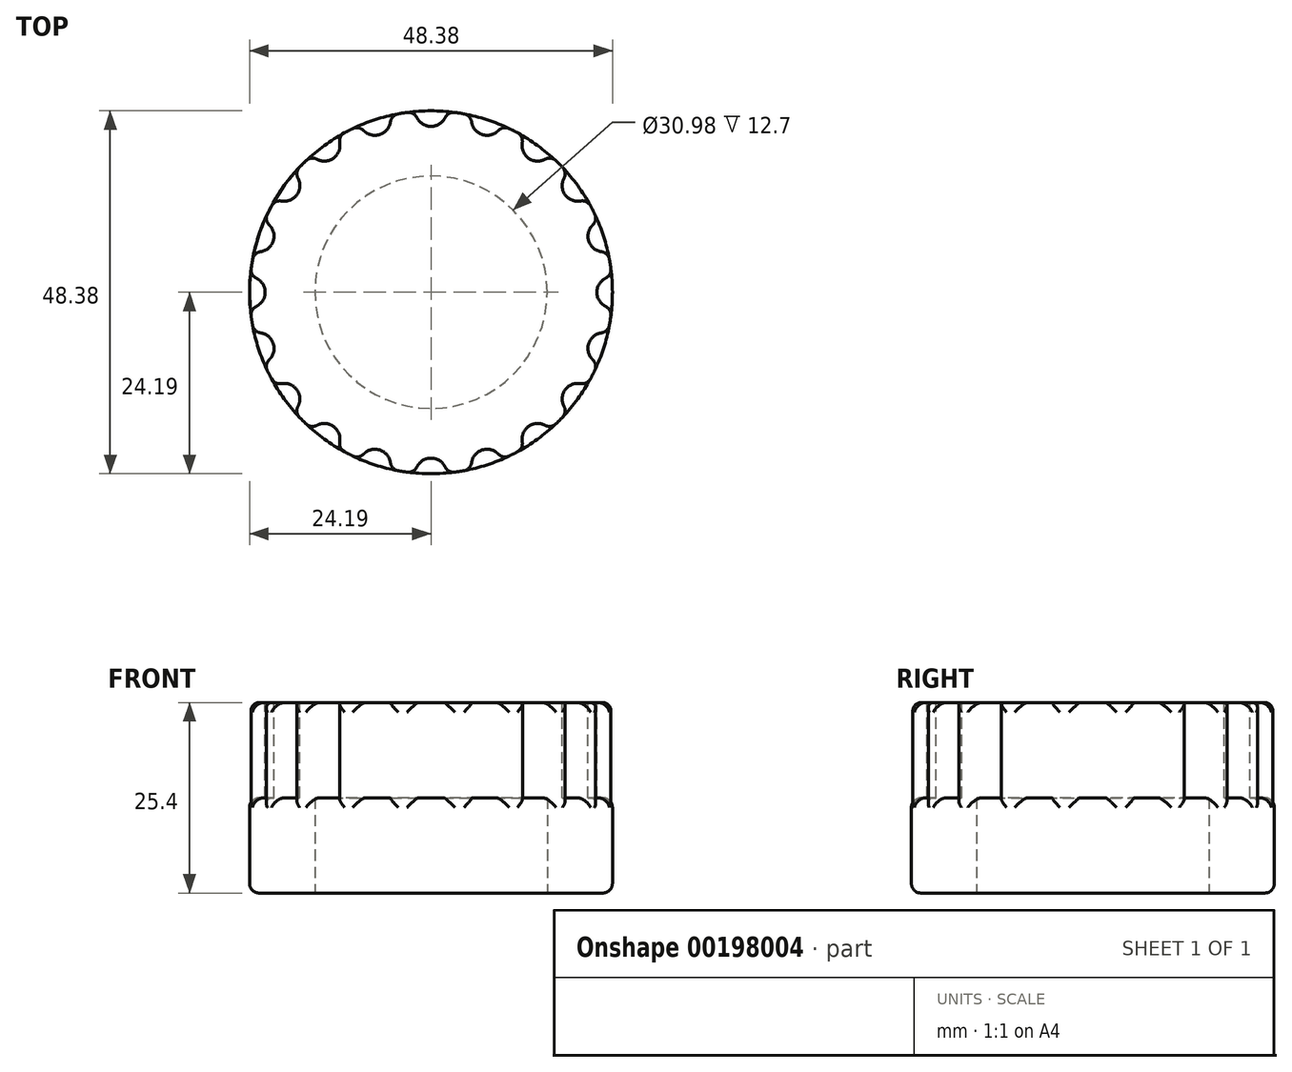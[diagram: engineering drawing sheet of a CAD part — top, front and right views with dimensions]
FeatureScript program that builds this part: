
annotation { "Feature Type Name" : "Feature", "Feature Type Description" : "" }
export const myFeature = defineFeature(function(context is Context, id is Id, definition is map)
    precondition{}
    {
        {
            var Q0;
            Q0=qCreatedBy(makeId("Top.planeOp"),FACE);
            var sketch = newSketch(context, id + "F0", { "sketchPlane" : qUnion([Q0])});
            skCircle(sketch, "E0", {"center": v(0, 0) * mm, "radius": 15.5 * mm});
            skCircle(sketch, "E1", {"center": v(0, 0) * mm, "radius": 24.19 * mm});
            skSolve(sketch);
        }
        {
            var Q0;
            Q0 = qSketchRegion(id + "F0", true);
            extrude(context, id + "F1", {"entities" : qUnion([Q0]), "depth" : 12.7 * mm});
        }
        {
            var Q0;
            Q0=makeQuery(id+"F1.opExtrude","CAP_FACE",FACE,{"disambiguationData":[OSD([sQuery(id+"F0.wireOp",EDGE,"E0"),sQuery(id+"F0.wireOp",EDGE,"E1")])],"isStart":false});
            var sketch = newSketch(context, id + "F2", { "sketchPlane" : qUnion([Q0])});
            skCircle(sketch, "E2.0", {"center": v(0, 0) * mm, "radius": 24.19 * mm});
            skSolve(sketch);
        }
        {
            var Q0;
            Q0 = qSketchRegion(id + "F2", true);
            extrude(context, id + "F3", {"entities" : qUnion([Q0]), "operationType" : NewBodyOperationType.ADD, "depth" : 12.7 * mm});
        }
        {
            var Q0;
            Q0=makeQuery(id+"F3.opExtrude","CAP_FACE",FACE,{"disambiguationData":[OSD([sQuery(id+"F2.wireOp",EDGE,"E2.0")])],"isStart":false});
            var sketch = newSketch(context, id + "F4", { "sketchPlane" : qUnion([Q0])});
            skLineSegment(sketch, "E3", {"start": v(0, 0) * mm, "end": v(0, 24.19) * mm, "construction": true});
            skCircle(sketch, "E4", {"center": v(0, 0) * mm, "radius": 22.1 * mm, "construction": true});
            skCircle(sketch, "E5", {"center": v(0, 24.19) * mm, "radius": 2.08 * mm});
            skCircle(sketch, "E6.1.0", {"center": v(-7.47, 23) * mm, "radius": 2.08 * mm});
            skCircle(sketch, "E6.2.0", {"center": v(-14.22, 19.57) * mm, "radius": 2.08 * mm});
            skCircle(sketch, "E6.3.0", {"center": v(-19.57, 14.22) * mm, "radius": 2.08 * mm});
            skCircle(sketch, "E6.4.0", {"center": v(-23, 7.47) * mm, "radius": 2.08 * mm});
            skCircle(sketch, "E6.5.0", {"center": v(-24.19, 0) * mm, "radius": 2.08 * mm});
            skCircle(sketch, "E6.6.0", {"center": v(-23, -7.47) * mm, "radius": 2.08 * mm});
            skCircle(sketch, "E6.7.0", {"center": v(-19.57, -14.22) * mm, "radius": 2.08 * mm});
            skCircle(sketch, "E6.8.0", {"center": v(-14.22, -19.57) * mm, "radius": 2.08 * mm});
            skCircle(sketch, "E6.9.0", {"center": v(-7.47, -23) * mm, "radius": 2.08 * mm});
            skCircle(sketch, "E7.1.10.0", {"center": v(0, -24.19) * mm, "radius": 2.08 * mm});
            skCircle(sketch, "E8.1.11.0", {"center": v(7.47, -23) * mm, "radius": 2.08 * mm});
            skCircle(sketch, "E9.1.12.0", {"center": v(14.22, -19.57) * mm, "radius": 2.08 * mm});
            skCircle(sketch, "E9.1.13.0", {"center": v(19.57, -14.22) * mm, "radius": 2.08 * mm});
            skCircle(sketch, "E9.1.14.0", {"center": v(23, -7.47) * mm, "radius": 2.08 * mm});
            skCircle(sketch, "E10.1.15.0", {"center": v(24.19, 0) * mm, "radius": 2.08 * mm});
            skCircle(sketch, "E10.1.16.0", {"center": v(23, 7.47) * mm, "radius": 2.08 * mm});
            skCircle(sketch, "E10.1.17.0", {"center": v(19.57, 14.22) * mm, "radius": 2.08 * mm});
            skCircle(sketch, "E10.1.18.0", {"center": v(14.22, 19.57) * mm, "radius": 2.08 * mm});
            skCircle(sketch, "E10.1.19.0", {"center": v(7.47, 23) * mm, "radius": 2.08 * mm});
            skSolve(sketch);
        }
        {
            var Q0;
            {var subQ0=sQuery(id+"F4.wireOp",EDGE,"E5");var subQ1=makeQuery(id+"F3.opExtrude","CAP_EDGE",EDGE,{"disambiguationData":[OSD([sQuery(id+"F2.wireOp",EDGE,"E2.0")])],"isStart":false});var subQ2=makeQuery(id+"F4.imprint","INTERSECT",VERTEX,{"disambiguationData":[OD(0.0)],"derivedFrom":[subQ1,subQ0]});Q0=makeQuery(id+"F4.imprint","IMPRINT",FACE,{"disambiguationData":[TD([[makeQuery(id+"F4.imprint","IMPRINT",EDGE,{"disambiguationData":[TD([[subQ2,-1.0]])],"derivedFrom":subQ0}),1.0]])]});}
            var Q1;
            {var subQ0=sQuery(id+"F4.wireOp",EDGE,"E6.1.0");var subQ1=makeQuery(id+"F3.opExtrude","CAP_EDGE",EDGE,{"disambiguationData":[OSD([sQuery(id+"F2.wireOp",EDGE,"E2.0")])],"isStart":false});var subQ2=makeQuery(id+"F4.imprint","INTERSECT",VERTEX,{"disambiguationData":[OD(0.0)],"derivedFrom":[subQ1,subQ0]});Q1=makeQuery(id+"F4.imprint","IMPRINT",FACE,{"disambiguationData":[TD([[makeQuery(id+"F4.imprint","IMPRINT",EDGE,{"disambiguationData":[TD([[subQ2,-1.0]])],"derivedFrom":subQ0}),1.0]])]});}
            var Q2;
            {var subQ0=sQuery(id+"F4.wireOp",EDGE,"E6.2.0");var subQ1=makeQuery(id+"F3.opExtrude","CAP_EDGE",EDGE,{"disambiguationData":[OSD([sQuery(id+"F2.wireOp",EDGE,"E2.0")])],"isStart":false});var subQ2=makeQuery(id+"F4.imprint","INTERSECT",VERTEX,{"disambiguationData":[OD(0.0)],"derivedFrom":[subQ1,subQ0]});Q2=makeQuery(id+"F4.imprint","IMPRINT",FACE,{"disambiguationData":[TD([[makeQuery(id+"F4.imprint","IMPRINT",EDGE,{"disambiguationData":[TD([[subQ2,-1.0]])],"derivedFrom":subQ0}),1.0]])]});}
            var Q3;
            {var subQ0=sQuery(id+"F4.wireOp",EDGE,"E6.3.0");var subQ1=makeQuery(id+"F3.opExtrude","CAP_EDGE",EDGE,{"disambiguationData":[OSD([sQuery(id+"F2.wireOp",EDGE,"E2.0")])],"isStart":false});var subQ2=makeQuery(id+"F4.imprint","INTERSECT",VERTEX,{"disambiguationData":[OD(0.0)],"derivedFrom":[subQ1,subQ0]});Q3=makeQuery(id+"F4.imprint","IMPRINT",FACE,{"disambiguationData":[TD([[makeQuery(id+"F4.imprint","IMPRINT",EDGE,{"disambiguationData":[TD([[subQ2,-1.0]])],"derivedFrom":subQ0}),1.0]])]});}
            var Q4;
            {var subQ0=sQuery(id+"F4.wireOp",EDGE,"E6.4.0");var subQ1=makeQuery(id+"F3.opExtrude","CAP_EDGE",EDGE,{"disambiguationData":[OSD([sQuery(id+"F2.wireOp",EDGE,"E2.0")])],"isStart":false});var subQ2=makeQuery(id+"F4.imprint","INTERSECT",VERTEX,{"disambiguationData":[OD(0.0)],"derivedFrom":[subQ1,subQ0]});Q4=makeQuery(id+"F4.imprint","IMPRINT",FACE,{"disambiguationData":[TD([[makeQuery(id+"F4.imprint","IMPRINT",EDGE,{"disambiguationData":[TD([[subQ2,-1.0]])],"derivedFrom":subQ0}),1.0]])]});}
            var Q5;
            {var subQ0=sQuery(id+"F4.wireOp",EDGE,"E6.5.0");var subQ1=makeQuery(id+"F3.opExtrude","CAP_EDGE",EDGE,{"disambiguationData":[OSD([sQuery(id+"F2.wireOp",EDGE,"E2.0")])],"isStart":false});var subQ2=makeQuery(id+"F4.imprint","INTERSECT",VERTEX,{"disambiguationData":[OD(0.0)],"derivedFrom":[subQ1,subQ0]});Q5=makeQuery(id+"F4.imprint","IMPRINT",FACE,{"disambiguationData":[TD([[makeQuery(id+"F4.imprint","IMPRINT",EDGE,{"disambiguationData":[TD([[subQ2,-1.0]])],"derivedFrom":subQ0}),1.0]])]});}
            var Q6;
            {var subQ0=sQuery(id+"F4.wireOp",EDGE,"E6.6.0");var subQ1=makeQuery(id+"F3.opExtrude","CAP_EDGE",EDGE,{"disambiguationData":[OSD([sQuery(id+"F2.wireOp",EDGE,"E2.0")])],"isStart":false});var subQ2=makeQuery(id+"F4.imprint","INTERSECT",VERTEX,{"disambiguationData":[OD(0.0)],"derivedFrom":[subQ1,subQ0]});Q6=makeQuery(id+"F4.imprint","IMPRINT",FACE,{"disambiguationData":[TD([[makeQuery(id+"F4.imprint","IMPRINT",EDGE,{"disambiguationData":[TD([[subQ2,-1.0]])],"derivedFrom":subQ0}),1.0]])]});}
            var Q7;
            {var subQ0=sQuery(id+"F4.wireOp",EDGE,"E6.7.0");var subQ1=makeQuery(id+"F3.opExtrude","CAP_EDGE",EDGE,{"disambiguationData":[OSD([sQuery(id+"F2.wireOp",EDGE,"E2.0")])],"isStart":false});var subQ2=makeQuery(id+"F4.imprint","INTERSECT",VERTEX,{"disambiguationData":[OD(0.0)],"derivedFrom":[subQ1,subQ0]});Q7=makeQuery(id+"F4.imprint","IMPRINT",FACE,{"disambiguationData":[TD([[makeQuery(id+"F4.imprint","IMPRINT",EDGE,{"disambiguationData":[TD([[subQ2,1.0]])],"derivedFrom":subQ0}),1.0]])]});}
            var Q8;
            {var subQ0=sQuery(id+"F4.wireOp",EDGE,"E6.8.0");var subQ1=makeQuery(id+"F3.opExtrude","CAP_EDGE",EDGE,{"disambiguationData":[OSD([sQuery(id+"F2.wireOp",EDGE,"E2.0")])],"isStart":false});var subQ2=makeQuery(id+"F4.imprint","INTERSECT",VERTEX,{"disambiguationData":[OD(0.0)],"derivedFrom":[subQ1,subQ0]});Q8=makeQuery(id+"F4.imprint","IMPRINT",FACE,{"disambiguationData":[TD([[makeQuery(id+"F4.imprint","IMPRINT",EDGE,{"disambiguationData":[TD([[subQ2,1.0]])],"derivedFrom":subQ0}),1.0]])]});}
            var Q9;
            {var subQ0=sQuery(id+"F4.wireOp",EDGE,"E6.9.0");var subQ1=makeQuery(id+"F3.opExtrude","CAP_EDGE",EDGE,{"disambiguationData":[OSD([sQuery(id+"F2.wireOp",EDGE,"E2.0")])],"isStart":false});var subQ2=makeQuery(id+"F4.imprint","INTERSECT",VERTEX,{"disambiguationData":[OD(0.0)],"derivedFrom":[subQ1,subQ0]});Q9=makeQuery(id+"F4.imprint","IMPRINT",FACE,{"disambiguationData":[TD([[makeQuery(id+"F4.imprint","IMPRINT",EDGE,{"disambiguationData":[TD([[subQ2,1.0]])],"derivedFrom":subQ0}),1.0]])]});}
            var Q10;
            {var subQ0=sQuery(id+"F4.wireOp",EDGE,"E7.1.10.0");var subQ1=makeQuery(id+"F3.opExtrude","CAP_EDGE",EDGE,{"disambiguationData":[OSD([sQuery(id+"F2.wireOp",EDGE,"E2.0")])],"isStart":false});var subQ2=makeQuery(id+"F4.imprint","INTERSECT",VERTEX,{"disambiguationData":[OD(0.0)],"derivedFrom":[subQ1,subQ0]});Q10=makeQuery(id+"F4.imprint","IMPRINT",FACE,{"disambiguationData":[TD([[makeQuery(id+"F4.imprint","IMPRINT",EDGE,{"disambiguationData":[TD([[subQ2,1.0]])],"derivedFrom":subQ0}),1.0]])]});}
            var Q11;
            {var subQ0=sQuery(id+"F4.wireOp",EDGE,"E8.1.11.0");var subQ1=makeQuery(id+"F3.opExtrude","CAP_EDGE",EDGE,{"disambiguationData":[OSD([sQuery(id+"F2.wireOp",EDGE,"E2.0")])],"isStart":false});var subQ2=makeQuery(id+"F4.imprint","INTERSECT",VERTEX,{"disambiguationData":[OD(0.0)],"derivedFrom":[subQ1,subQ0]});Q11=makeQuery(id+"F4.imprint","IMPRINT",FACE,{"disambiguationData":[TD([[makeQuery(id+"F4.imprint","IMPRINT",EDGE,{"disambiguationData":[TD([[subQ2,1.0]])],"derivedFrom":subQ0}),1.0]])]});}
            var Q12;
            {var subQ0=sQuery(id+"F4.wireOp",EDGE,"E9.1.12.0");var subQ1=makeQuery(id+"F3.opExtrude","CAP_EDGE",EDGE,{"disambiguationData":[OSD([sQuery(id+"F2.wireOp",EDGE,"E2.0")])],"isStart":false});var subQ2=makeQuery(id+"F4.imprint","INTERSECT",VERTEX,{"disambiguationData":[OD(0.0)],"derivedFrom":[subQ1,subQ0]});Q12=makeQuery(id+"F4.imprint","IMPRINT",FACE,{"disambiguationData":[TD([[makeQuery(id+"F4.imprint","IMPRINT",EDGE,{"disambiguationData":[TD([[subQ2,1.0]])],"derivedFrom":subQ0}),1.0]])]});}
            var Q13;
            {var subQ0=sQuery(id+"F4.wireOp",EDGE,"E9.1.13.0");var subQ1=makeQuery(id+"F3.opExtrude","CAP_EDGE",EDGE,{"disambiguationData":[OSD([sQuery(id+"F2.wireOp",EDGE,"E2.0")])],"isStart":false});var subQ2=makeQuery(id+"F4.imprint","INTERSECT",VERTEX,{"disambiguationData":[OD(0.0)],"derivedFrom":[subQ1,subQ0]});Q13=makeQuery(id+"F4.imprint","IMPRINT",FACE,{"disambiguationData":[TD([[makeQuery(id+"F4.imprint","IMPRINT",EDGE,{"disambiguationData":[TD([[subQ2,1.0]])],"derivedFrom":subQ0}),1.0]])]});}
            var Q14;
            {var subQ0=sQuery(id+"F4.wireOp",EDGE,"E9.1.14.0");var subQ1=makeQuery(id+"F3.opExtrude","CAP_EDGE",EDGE,{"disambiguationData":[OSD([sQuery(id+"F2.wireOp",EDGE,"E2.0")])],"isStart":false});var subQ2=makeQuery(id+"F4.imprint","INTERSECT",VERTEX,{"disambiguationData":[OD(0.0)],"derivedFrom":[subQ1,subQ0]});Q14=makeQuery(id+"F4.imprint","IMPRINT",FACE,{"disambiguationData":[TD([[makeQuery(id+"F4.imprint","IMPRINT",EDGE,{"disambiguationData":[TD([[subQ2,1.0]])],"derivedFrom":subQ0}),1.0]])]});}
            var Q15;
            {var subQ0=sQuery(id+"F4.wireOp",EDGE,"E10.1.15.0");var subQ1=makeQuery(id+"F3.opExtrude","CAP_EDGE",EDGE,{"disambiguationData":[OSD([sQuery(id+"F2.wireOp",EDGE,"E2.0")])],"isStart":false});var subQ2=makeQuery(id+"F4.imprint","INTERSECT",VERTEX,{"disambiguationData":[OD(0.0)],"derivedFrom":[subQ1,subQ0]});Q15=makeQuery(id+"F4.imprint","IMPRINT",FACE,{"disambiguationData":[TD([[makeQuery(id+"F4.imprint","IMPRINT",EDGE,{"disambiguationData":[TD([[subQ2,1.0]])],"derivedFrom":subQ0}),1.0]])]});}
            var Q16;
            {var subQ0=sQuery(id+"F4.wireOp",EDGE,"E10.1.16.0");var subQ1=makeQuery(id+"F3.opExtrude","CAP_EDGE",EDGE,{"disambiguationData":[OSD([sQuery(id+"F2.wireOp",EDGE,"E2.0")])],"isStart":false});var subQ2=makeQuery(id+"F4.imprint","INTERSECT",VERTEX,{"disambiguationData":[OD(0.0)],"derivedFrom":[subQ1,subQ0]});Q16=makeQuery(id+"F4.imprint","IMPRINT",FACE,{"disambiguationData":[TD([[makeQuery(id+"F4.imprint","IMPRINT",EDGE,{"disambiguationData":[TD([[subQ2,1.0]])],"derivedFrom":subQ0}),1.0]])]});}
            var Q17;
            {var subQ0=sQuery(id+"F4.wireOp",EDGE,"E10.1.17.0");var subQ1=makeQuery(id+"F3.opExtrude","CAP_EDGE",EDGE,{"disambiguationData":[OSD([sQuery(id+"F2.wireOp",EDGE,"E2.0")])],"isStart":false});var subQ2=makeQuery(id+"F4.imprint","INTERSECT",VERTEX,{"disambiguationData":[OD(0.0)],"derivedFrom":[subQ1,subQ0]});Q17=makeQuery(id+"F4.imprint","IMPRINT",FACE,{"disambiguationData":[TD([[makeQuery(id+"F4.imprint","IMPRINT",EDGE,{"disambiguationData":[TD([[subQ2,-1.0]])],"derivedFrom":subQ0}),1.0]])]});}
            var Q18;
            {var subQ0=sQuery(id+"F4.wireOp",EDGE,"E10.1.18.0");var subQ1=makeQuery(id+"F3.opExtrude","CAP_EDGE",EDGE,{"disambiguationData":[OSD([sQuery(id+"F2.wireOp",EDGE,"E2.0")])],"isStart":false});var subQ2=makeQuery(id+"F4.imprint","INTERSECT",VERTEX,{"disambiguationData":[OD(0.0)],"derivedFrom":[subQ1,subQ0]});Q18=makeQuery(id+"F4.imprint","IMPRINT",FACE,{"disambiguationData":[TD([[makeQuery(id+"F4.imprint","IMPRINT",EDGE,{"disambiguationData":[TD([[subQ2,-1.0]])],"derivedFrom":subQ0}),1.0]])]});}
            var Q19;
            {var subQ0=sQuery(id+"F4.wireOp",EDGE,"E10.1.19.0");var subQ1=makeQuery(id+"F3.opExtrude","CAP_EDGE",EDGE,{"disambiguationData":[OSD([sQuery(id+"F2.wireOp",EDGE,"E2.0")])],"isStart":false});var subQ2=makeQuery(id+"F4.imprint","INTERSECT",VERTEX,{"disambiguationData":[OD(0.0)],"derivedFrom":[subQ1,subQ0]});Q19=makeQuery(id+"F4.imprint","IMPRINT",FACE,{"disambiguationData":[TD([[makeQuery(id+"F4.imprint","IMPRINT",EDGE,{"disambiguationData":[TD([[subQ2,-1.0]])],"derivedFrom":subQ0}),1.0]])]});}
            var Q20;
            Q20=makeQuery(id+"F3.opExtrude","CAP_FACE",FACE,{"disambiguationData":[OSD([sQuery(id+"F2.wireOp",EDGE,"E2.0")])],"isStart":true});
            extrude(context, id + "F5", {"entities" : qUnion([Q0, Q1, Q2, Q3, Q4, Q5, Q6, Q7, Q8, Q9, Q10, Q11, Q12, Q13, Q14, Q15, Q16, Q17, Q18, Q19]), "operationType" : NewBodyOperationType.REMOVE, "endBound" : BoundingType.UP_TO_SURFACE, "oppositeDirection" : true, "endBoundEntityFace" : qUnion([Q20]), "depth" : 12.7 * mm});
        }
        {
            var Q0;
            Q0=makeQuery(id+"F3.boolean.opBoolean","MERGE",FACE,{"derivedFrom":[makeQuery(id+"F1.opExtrude","SWEPT_FACE",FACE,{"disambiguationData":[OSD([sQuery(id+"F0.wireOp",EDGE,"E1")])]}),makeQuery(id+"F3.opExtrude","SWEPT_FACE",FACE,{"disambiguationData":[OSD([sQuery(id+"F2.wireOp",EDGE,"E2.0")])]})]});
            fillet(context, id + "F6", {"entities" : qUnion([Q0]), "radius" : 1.27 * mm, "tangentPropagation" : true, "allowEdgeOverflow" : false});
        }
    });
